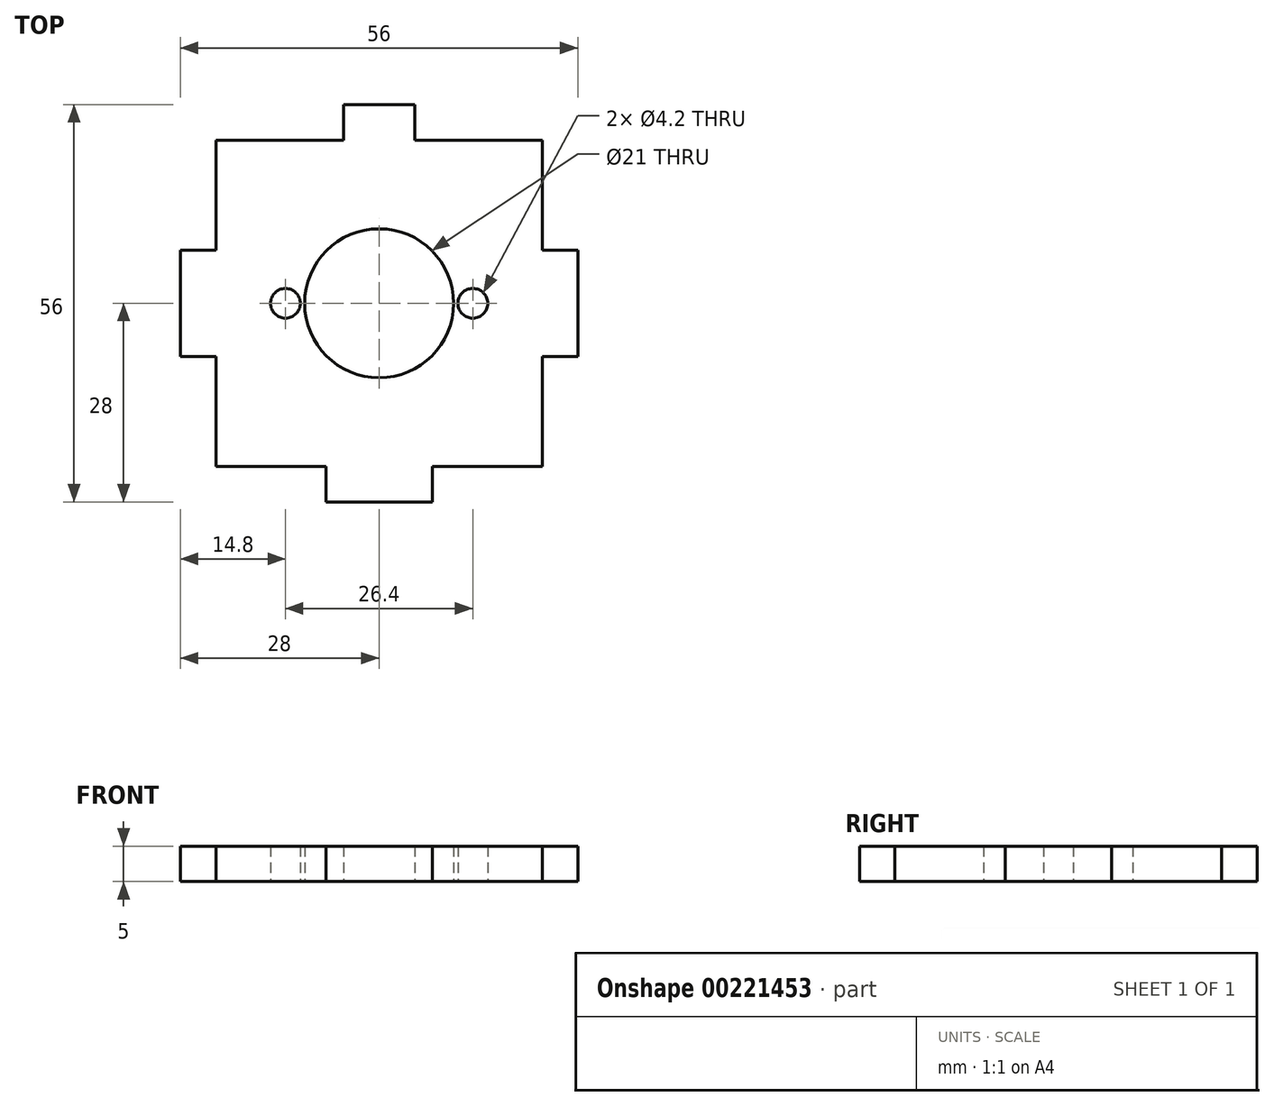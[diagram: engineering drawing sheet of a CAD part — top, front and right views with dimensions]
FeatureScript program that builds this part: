
annotation { "Feature Type Name" : "Feature", "Feature Type Description" : "" }
export const myFeature = defineFeature(function(context is Context, id is Id, definition is map)
    precondition{}
    {
        {
            assignVariable(context, id + "F0", {"name" : "thickness", "anyValue" : 5 * mm});
        }
        {
            var Q0;
            Q0=qCreatedBy(makeId("Top.planeOp"),FACE);
            var sketch = newSketch(context, id + "F1", { "sketchPlane" : qUnion([Q0])});
            skLineSegment(sketch, "E0.bottom", {"start": v(0, 0) * mm, "end": v(15.5, 0) * mm});
            skLineSegment(sketch, "E0.top", {"start": v(0, 46) * mm, "end": v(18, 46) * mm});
            skLineSegment(sketch, "E0.left", {"start": v(0, 0) * mm, "end": v(0, 15.5) * mm});
            skLineSegment(sketch, "E0.right", {"start": v(46, 0) * mm, "end": v(46, 15.5) * mm});
            skCircle(sketch, "E1", {"center": v(23, 23) * mm, "radius": 13.2 * mm, "construction": true});
            skPoint(sketch, "E1.centerSnap0", {"position": v(0, 23) * mm});
            skPoint(sketch, "E1.centerSnap1", {"position": v(23, 46) * mm});
            skCircle(sketch, "E2", {"center": v(23, 23) * mm, "radius": 10.5 * mm});
            skLineSegment(sketch, "E3", {"start": v(18, 46) * mm, "end": v(18, 51) * mm});
            skLineSegment(sketch, "E4", {"start": v(18, 51) * mm, "end": v(28, 51) * mm});
            skLineSegment(sketch, "E5", {"start": v(28, 51) * mm, "end": v(28, 46) * mm});
            skPoint(sketch, "E6", {"position": v(23, 51) * mm});
            skLineSegment(sketch, "E7.trimOffspring", {"start": v(28, 46) * mm, "end": v(46, 46) * mm});
            skLineSegment(sketch, "E8", {"start": v(0, 30.5) * mm, "end": v(-5, 30.5) * mm});
            skLineSegment(sketch, "E9", {"start": v(-5, 30.5) * mm, "end": v(-5, 15.5) * mm});
            skLineSegment(sketch, "E10", {"start": v(-5, 15.5) * mm, "end": v(0, 15.5) * mm});
            skPoint(sketch, "E11", {"position": v(-5, 23) * mm});
            skLineSegment(sketch, "E12", {"start": v(23, 51) * mm, "end": v(23, 0) * mm, "construction": true});
            skPoint(sketch, "E13.MirrorP", {"position": v(46, 23) * mm});
            skLineSegment(sketch, "E14.MirrorCS", {"start": v(51, 15.5) * mm, "end": v(46, 15.5) * mm});
            skLineSegment(sketch, "E15.MirrorCS", {"start": v(51, 30.5) * mm, "end": v(51, 15.5) * mm});
            skLineSegment(sketch, "E16.MirrorCS", {"start": v(46, 30.5) * mm, "end": v(51, 30.5) * mm});
            skPoint(sketch, "E17.MirrorP", {"position": v(51, 23) * mm});
            skLineSegment(sketch, "E18.trimOffspring", {"start": v(0, 30.5) * mm, "end": v(0, 46) * mm});
            skLineSegment(sketch, "E19.trimOffspring", {"start": v(46, 30.5) * mm, "end": v(46, 46) * mm});
            skLineSegment(sketch, "E20", {"start": v(0, 0) * mm, "end": v(46, 46) * mm, "construction": true});
            skPoint(sketch, "E21.MirrorP", {"position": v(23, 0) * mm});
            skLineSegment(sketch, "E22.MirrorCS", {"start": v(15.5, -5) * mm, "end": v(15.5, 0) * mm});
            skLineSegment(sketch, "E23.MirrorCS", {"start": v(30.5, -5) * mm, "end": v(15.5, -5) * mm});
            skLineSegment(sketch, "E24.MirrorCS", {"start": v(30.5, 0) * mm, "end": v(30.5, -5) * mm});
            skPoint(sketch, "E25.MirrorP", {"position": v(23, -5) * mm});
            skLineSegment(sketch, "E26.trimOffspring", {"start": v(30.5, 0) * mm, "end": v(46, 0) * mm});
            skCircle(sketch, "E27", {"center": v(9.8, 23) * mm, "radius": 2.1 * mm});
            skCircle(sketch, "E28.MirrorC", {"center": v(36.2, 23) * mm, "radius": 2.1 * mm});
            skSolve(sketch);
        }
        {
            var Q0;
            Q0 = qSketchRegion(id + "F1", true);
            extrude(context, id + "F2", {"entities" : qUnion([Q0]), "depth" : getVariable(context, 'thickness')});
        }
    });
